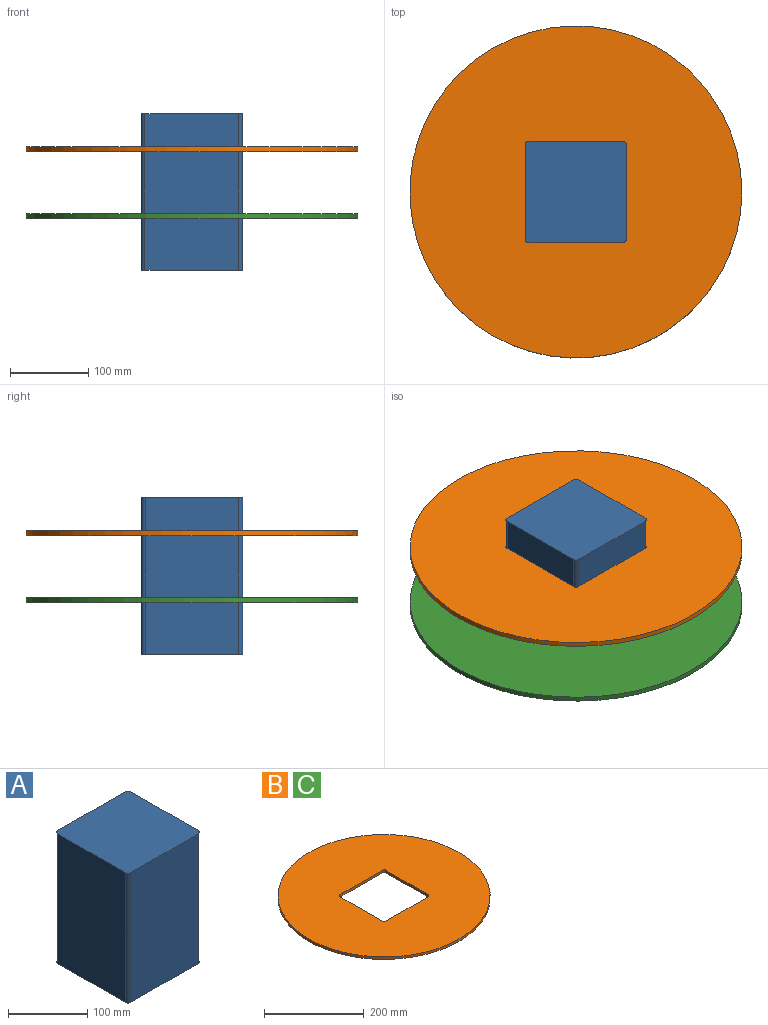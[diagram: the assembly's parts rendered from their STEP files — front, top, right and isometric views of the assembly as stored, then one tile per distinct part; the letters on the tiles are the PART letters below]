
ASSEMBLY  parts=3 mates=2
PART A: 10 faces, bbox 130x130x200 mm
  f0: plane 200x120mm, normal (0,-1,0), area 24000mm2, adj f4,f5,f6,f9
  f1: plane 200x120mm, normal (1,0,0), area 24000mm2, adj f4,f5,f6,f7
  f2: plane 200x120mm, normal (0,1,0), area 24000mm2, adj f4,f5,f7,f8
  f3: plane 200x120mm, normal (-1,0,0), area 24000mm2, adj f4,f5,f8,f9
  f4: plane 130x130mm, normal (0,0,1), area 16878.5mm2, adj f0,f1,f2,f3,f6,f7,f8,f9
  f5: plane 130x130mm, normal (0,0,-1), area 16878.5mm2, adj f0,f1,f2,f3,f6,f7,f8,f9
  f6: cylinder r=5mm len=200mm, axis (0,0,1), area 1570.8mm2, adj f0,f1,f4,f5
  f7: cylinder r=5mm len=200mm, axis (0,0,-1), area 1570.8mm2, adj f1,f2,f4,f5
  f8: cylinder r=5mm len=200mm, axis (0,0,1), area 1570.8mm2, adj f2,f3,f4,f5
  f9: cylinder r=5mm len=200mm, axis (0,0,-1), area 1570.8mm2, adj f0,f3,f4,f5
PART B: 11 faces, bbox 425x425x6 mm
  f0: plane 120x6mm, normal (-1,0,0), area 720mm2, adj f5,f6,f7,f10
  f1: plane 120x6mm, normal (0,1,0), area 720mm2, adj f5,f6,f7,f8
  f2: plane 120x6mm, normal (1,0,0), area 720mm2, adj f5,f6,f8,f9
  f3: plane 120x6mm, normal (0,-1,0), area 720mm2, adj f5,f6,f9,f10
  f4: cylinder r=212.5mm len=425mm, axis (0,0,-1), area 8011.1mm2, adj f5,f6
  f5: plane 425x425mm, normal (0,0,1), area 124984mm2, adj f0,f1,f2,f3,f4,f7,f8,f9
  f6: plane 425x425mm, normal (0,0,-1), area 124984mm2, adj f0,f1,f2,f3,f4,f7,f8,f9
  f7: cylinder r=5mm len=6mm, axis (0,0,-1), area 47.1mm2, adj f0,f1,f5,f6
  f8: cylinder r=5mm len=6mm, axis (0,0,1), area 47.1mm2, adj f1,f2,f5,f6
  f9: cylinder r=5mm len=6mm, axis (0,0,-1), area 47.1mm2, adj f2,f3,f5,f6
  f10: cylinder r=5mm len=6mm, axis (0,0,1), area 47.1mm2, adj f0,f3,f5,f6
PART C: same geometry as B
PLACE A t=(68.66,98.25,-94.72)mm fixed
PLACE B t=(68.66,98.25,56.93)mm
PLACE C t=(68.66,98.25,-28.83)mm
MATE slider A.f4 <-> B.f4  axis (0,0,1) through (68.66,98.25,105.28)mm
MATE slider A.f4 <-> C.f4  axis (0,0,1) through (68.66,98.25,105.28)mm
